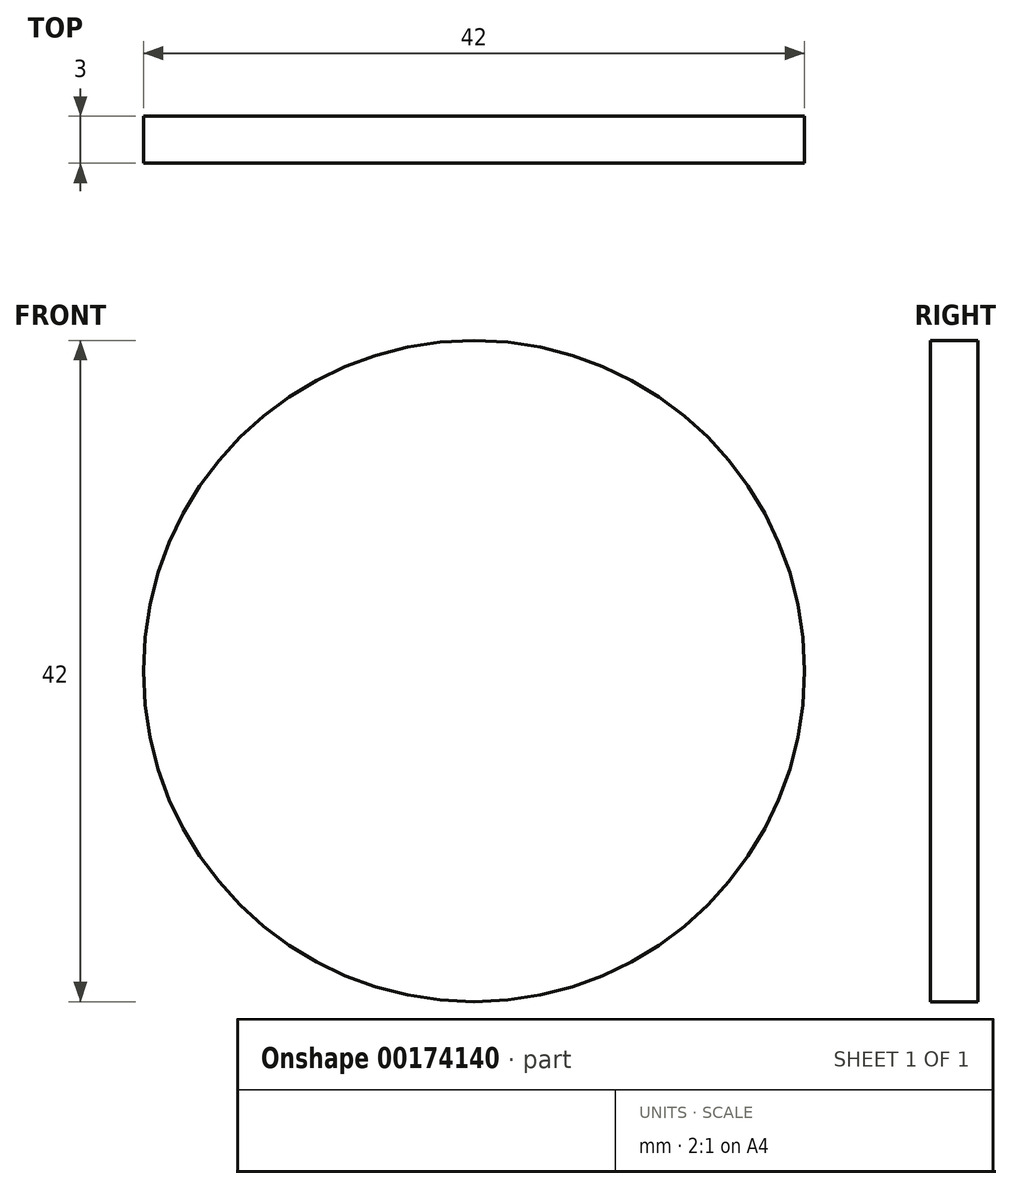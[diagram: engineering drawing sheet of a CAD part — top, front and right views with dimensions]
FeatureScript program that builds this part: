
annotation { "Feature Type Name" : "Feature", "Feature Type Description" : "" }
export const myFeature = defineFeature(function(context is Context, id is Id, definition is map)
    precondition{}
    {
        {
            var Q0;
            Q0=qCreatedBy(makeId("Front.planeOp"),FACE);
            var sketch = newSketch(context, id + "F0", { "sketchPlane" : qUnion([Q0])});
            skCircle(sketch, "E0", {"center": v(0, 0) * mm, "radius": 21 * mm});
            skSolve(sketch);
        }
        {
            var Q0;
            Q0=makeQuery(id+"F0.imprint","IMPRINT",FACE,{"disambiguationData":[TD([[makeQuery(id+"F0.imprint","IMPRINT",EDGE,{"derivedFrom":sQuery(id+"F0.wireOp",EDGE,"E0")}),1.0]])]});
            extrude(context, id + "F1", {"entities" : qUnion([Q0]), "depth" : 3 * mm});
        }
        {
            var Q0;
            Q0=qCreatedBy(makeId("Front.planeOp"),FACE);
            var sketch = newSketch(context, id + "F2", { "sketchPlane" : qUnion([Q0])});
            skCircle(sketch, "E1", {"center": v(0, 28.62) * mm, "radius": 3.25 * mm});
            skCircle(sketch, "E2", {"center": v(0, 28.62) * mm, "radius": 2.2 * mm});
            skCircle(sketch, "E3", {"center": v(24.88, -14.2) * mm, "radius": 3.4 * mm});
            skCircle(sketch, "E4", {"center": v(24.88, -14.2) * mm, "radius": 2.22 * mm});
            skCircle(sketch, "E5", {"center": v(-24.8, -14.2) * mm, "radius": 3.22 * mm});
            skCircle(sketch, "E6", {"center": v(-24.8, -14.2) * mm, "radius": 2.1 * mm});
            skSolve(sketch);
        }
        {
            var Q0;
            Q0 = qSketchRegion(id + "F2", true);
            extrude(context, id + "F3", {"entities" : qUnion([Q0]), "operationType" : NewBodyOperationType.REMOVE, "oppositeDirection" : true, "depth" : 25 * mm});
        }
        {
            var Q0;
            Q0=qCreatedBy(makeId("Front.planeOp"),FACE);
            var sketch = newSketch(context, id + "F4", { "sketchPlane" : qUnion([Q0])});
            skCircle(sketch, "E7", {"center": v(0, 28.71) * mm, "radius": 3.42 * mm});
            skSolve(sketch);
        }
        {
            var Q0;
            Q0 = qSketchRegion(id + "F4", true);
            extrude(context, id + "F5", {"entities" : qUnion([Q0]), "operationType" : NewBodyOperationType.REMOVE, "oppositeDirection" : true, "depth" : 25 * mm});
        }
    });
